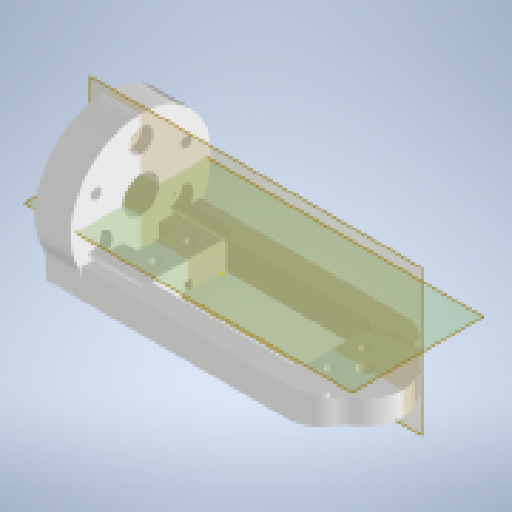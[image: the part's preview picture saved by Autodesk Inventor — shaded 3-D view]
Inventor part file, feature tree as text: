
AUTODESK INVENTOR PART (.ipt)
format: ipt  version: 2024 (Build 280153000, 153)  size: 425,984 bytes
history: native  units: mm
features: sketch x16, projected_geometry x12, extrude x10, fillet x5, hole x4, reference x4, other x3, plane x2
ambient origin geometry x8: Origin, YZ Plane, XZ Plane, XY Plane, X Axis, Y Axis, Z Axis, Center Point
bodies: Volumenkörper1 (feature_tree)
feature tree (56):
  extrude  "Extrusion1"  Depth=8.0mm TaperAngle=0.0deg
  hole  "Bohrung1"  [1 undecoded]
  extrude  "Extrusion2"  Depth=10.5mm
  extrude  "Extrusion3"  Depth=7.0mm
  sketch  "Skizze5"  dims[d16=6.0mm d18=39.0mm]
  hole  "Bohrung2"  [1 undecoded]
  extrude  "Extrusion4"  Depth=10.0mm TaperAngle=0.0deg
  extrude  "Extrusion5"  TaperAngle=120.0deg  [1 undecoded]
  sketch  "Skizze9"  dims[d33=10.0mm d34=0.0mm d35=1.5mm d36=0.0mm]
  fillet  "Rundung1"  [1 undecoded]
  fillet  "Rundung2"  Radius=2.5mm
  extrude  "Extrusion6"  Depth=1.5mm TaperAngle=0.0deg
  extrude  "Extrusion7"  Depth=10.0mm
  hole  "Bohrung3"  [1 undecoded]
  extrude  "Extrusion8"  Depth=25.0mm
  hole  "Bohrung4"  [1 undecoded]
  extrude  "Extrusion9"  Depth=4.0mm
  fillet  "Rundung3"  Radius=10.0mm
  fillet  "Rundung4"  Radius=5.0mm
  fillet  "Rundung5"  Radius=10.0mm
  plane  "Arbeitsebene1"
  extrude  "Extrusion10"  Depth=1.0mm
  other  "Verdickung1"
  other  "Verdickung2"
  plane  "Work Plane2"
  sketch  "Skizze1"  dims[d0=6.0mm d1=8.0mm d2=0.0mm]
  reference  "Referenz1"
  reference  "Referenz2"
  reference  "Referenz3"
  reference  "Referenz4"
  sketch  "Skizze2"  dims[d3=4.0mm d4=6.0mm d5=4.0mm d6=2.0mm d7=90.0deg d8=8.0mm d9=20.594885mm d10=39.0mm]
  projected_geometry  "Projizierte Kontur1"
  sketch  "Skizze3"  dims[d11=10.0mm d12=10.5mm]
  projected_geometry  "Projizierte Kontur2"
  sketch  "Skizze4"  dims[d13=10.0mm d14=0.0mm d15=7.0mm]
  projected_geometry  "Projizierte Kontur3"
  projected_geometry  "Projizierte Kontur4"
  sketch  "Skizze6"  dims[d19=17.0mm d20=10.0mm d21=0.0mm]
  sketch  "Skizze7"  dims[d22=26.0mm d23=120.0deg d24=120.0deg]
  projected_geometry  "Projizierte Kontur5"
  sketch  "Skizze8"  dims[d25=3.0mm d26=6.0mm d27=6.5mm d28=16.0mm d29=90.0deg d30=8.0mm d31=20.594885mm d32=2.5mm]
  projected_geometry  "Projizierte Kontur6"
  sketch  "Skizze10"  dims[d37=2.0mm d38=10.0mm]
  projected_geometry  "Projizierte Kontur7"
  sketch  "Skizze11"  dims[d39=7.0mm d40=3.0mm d41=0.0mm]
  projected_geometry  "Projizierte Kontur8"
  sketch  "Skizze12"  dims[d42=0.2mm d43=0.0mm d44=25.0mm]
  projected_geometry  "Projizierte Kontur9"
  sketch  "Skizze13"  dims[d45=3.0mm d46=6.0mm d47=6.0mm d48=16.0mm d49=90.0deg d50=8.0mm d51=20.594885mm d52=5.5mm]
  projected_geometry  "Projizierte Kontur10"
  sketch  "Skizze14"  dims[d53=5.0mm d54=0.0mm]
  projected_geometry  "Projizierte Kontur11"
  sketch  "Skizze15"  dims[d55=10.0mm d56=6.0mm d57=6.0mm d58=16.0mm d59=90.0deg d60=8.0mm d61=20.594885mm d62=4.0mm d63=10.0mm d64=5.0mm d65=0.0mm d66=10.0mm]
  projected_geometry  "Projizierte Kontur12"
  sketch  "Skizze17"  dims[d67=10.0mm d68=1.0mm d69=1.0mm d70=3.0mm d71=7.0mm d73=7.0mm d74=2.0mm d75=0.0mm d76=1.0mm d77=1.0mm d78=1.0mm d79=1.0mm d80=3.0mm d82=-17.0mm]
  other  "Schnittkanten projizieren1"
note: 6 required parameter values undecoded (feature->parameter linkage not recoverable at this tier; creation-order binding heuristic only, values carry confidence <= 0.55)
